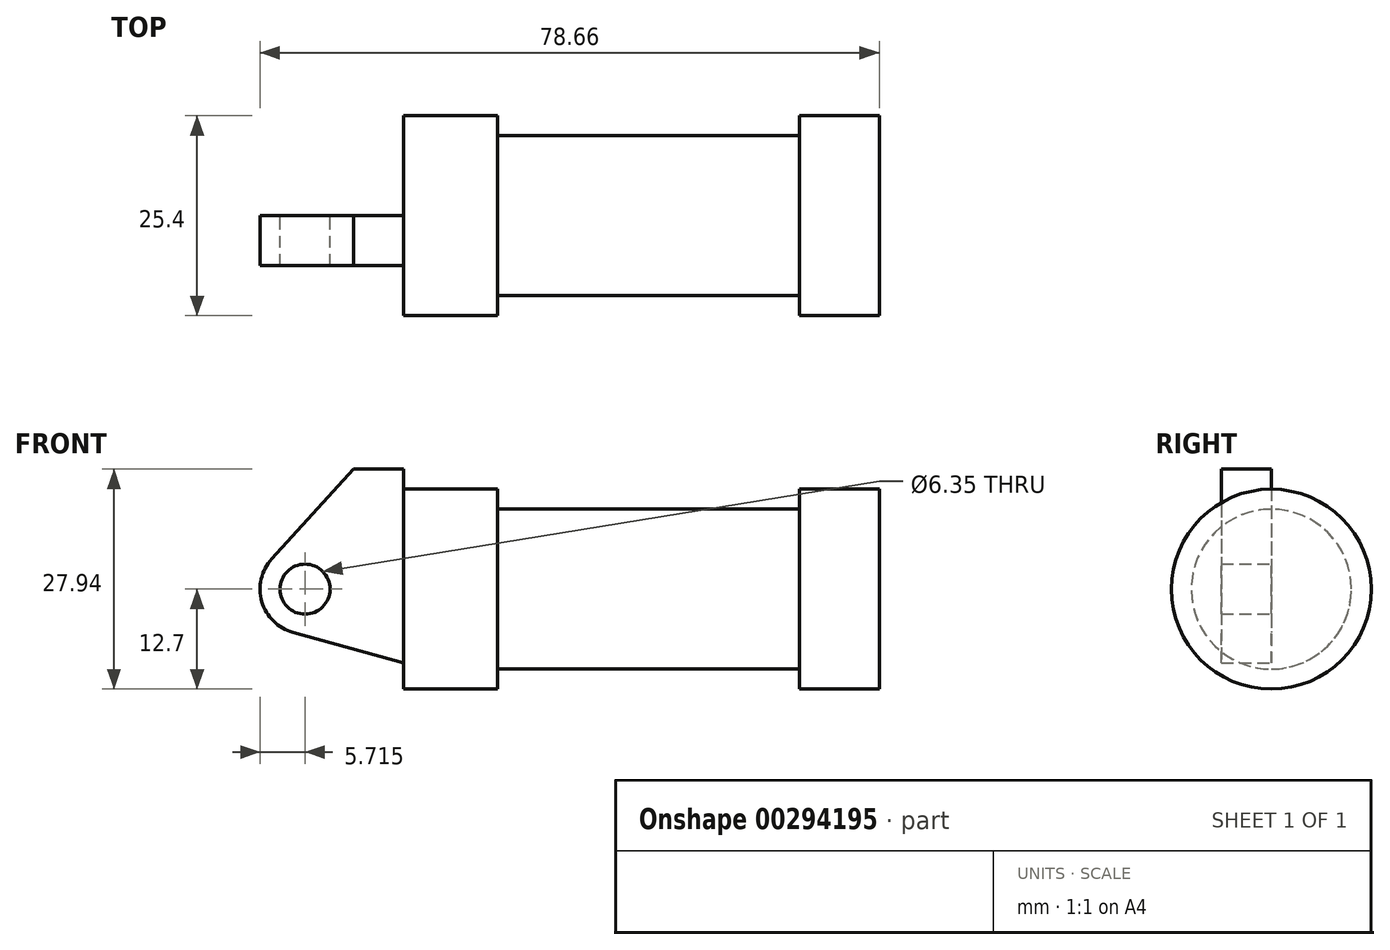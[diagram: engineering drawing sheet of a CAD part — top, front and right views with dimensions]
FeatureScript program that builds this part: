
annotation { "Feature Type Name" : "Feature", "Feature Type Description" : "" }
export const myFeature = defineFeature(function(context is Context, id is Id, definition is map)
    precondition{}
    {
        {
            var Q0;
            Q0=qCreatedBy(makeId("Front.planeOp"),FACE);
            var sketch = newSketch(context, id + "F0", { "sketchPlane" : qUnion([Q0])});
            skLineSegment(sketch, "E0", {"start": v(0, 0) * mm, "end": v(0, 12.7) * mm});
            skLineSegment(sketch, "E1", {"start": v(0, 12.7) * mm, "end": v(10.16, 12.7) * mm});
            skLineSegment(sketch, "E2", {"start": v(10.16, 12.7) * mm, "end": v(10.16, 10.16) * mm});
            skLineSegment(sketch, "E3", {"start": v(10.16, 10.16) * mm, "end": v(56.13, 10.16) * mm});
            skLineSegment(sketch, "E4", {"start": v(56.13, 10.16) * mm, "end": v(56.13, 12.7) * mm});
            skLineSegment(sketch, "E5", {"start": v(56.13, 12.7) * mm, "end": v(66.3, 12.7) * mm});
            skLineSegment(sketch, "E6", {"start": v(66.3, 12.7) * mm, "end": v(66.3, 0) * mm});
            skLineSegment(sketch, "E7", {"start": v(66.3, 0) * mm, "end": v(0, 0) * mm});
            skLineSegment(sketch, "E8", {"start": v(5.84, 15.24) * mm, "end": v(-0.5, 15.24) * mm});
            skLineSegment(sketch, "E9", {"start": v(-0.5, 15.24) * mm, "end": v(-10.88, 3.85) * mm});
            skLineSegment(sketch, "E10", {"start": v(0, 0) * mm, "end": v(-6.65, 0) * mm});
            skCircle(sketch, "E11", {"center": v(-6.65, 0) * mm, "radius": 5.72 * mm});
            skCircle(sketch, "E12", {"center": v(-6.65, 0) * mm, "radius": 3.18 * mm});
            skLineSegment(sketch, "E13", {"start": v(5.84, 15.24) * mm, "end": v(5.84, -9.4) * mm});
            skLineSegment(sketch, "E14", {"start": v(5.84, -9.4) * mm, "end": v(-8.18, -5.5) * mm});
            skSolve(sketch);
        }
        {
            var Q0;
            {var subQ0=sQuery(id+"F0.wireOp",EDGE,"E2");Q0=makeQuery(id+"F0.imprint","IMPRINT",FACE,{"disambiguationData":[TD([[makeQuery(id+"F0.imprint","IMPRINT",EDGE,{"derivedFrom":subQ0}),-1.0]])]});}
            var Q1;
            Q1=sQuery(id+"F0.wireOp",EDGE,"E7");
            revolve(context, id + "F1", {"entities" : qUnion([Q0]), "axis" : qUnion([Q1]), "revolveType" : RevolveType.FULL});
        }
        {
            var Q0;
            {var subQ5=sQuery(id+"F0.wireOp",EDGE,"E12");Q0=makeQuery(id+"F0.imprint","IMPRINT",FACE,{"disambiguationData":[TD([[makeQuery(id+"F0.imprint","IMPRINT",EDGE,{"derivedFrom":subQ5}),-1.0]])]});}
            var Q1;
            {var subQ0=sQuery(id+"F0.wireOp",EDGE,"E14");Q1=makeQuery(id+"F0.imprint","IMPRINT",FACE,{"disambiguationData":[TD([[makeQuery(id+"F0.imprint","IMPRINT",EDGE,{"derivedFrom":subQ0}),-1.0]])]});}
            var Q2;
            {var subQ1=sQuery(id+"F0.wireOp",EDGE,"E0");Q2=makeQuery(id+"F0.imprint","IMPRINT",FACE,{"disambiguationData":[TD([[makeQuery(id+"F0.imprint","IMPRINT",EDGE,{"derivedFrom":subQ1}),1.0]])]});}
            var Q3;
            {var subQ0=sQuery(id+"F0.wireOp",EDGE,"E0");Q3=makeQuery(id+"F0.imprint","IMPRINT",FACE,{"disambiguationData":[TD([[makeQuery(id+"F0.imprint","IMPRINT",EDGE,{"derivedFrom":subQ0}),-1.0]])]});}
            extrude(context, id + "F2", {"entities" : qUnion([Q0, Q1, Q2, Q3]), "operationType" : NewBodyOperationType.ADD, "depth" : 6.35 * mm});
        }
        {
            var Q0;
            Q0=makeQuery(id+"F1.opRevolve","SWEPT_FACE",FACE,{"disambiguationData":[OSD([sQuery(id+"F0.wireOp",EDGE,"E2")])]});
            extrude(context, id + "F3", {"entities" : qUnion([Q0]), "operationType" : NewBodyOperationType.ADD, "depth" : 7.62 * mm});
        }
    });
